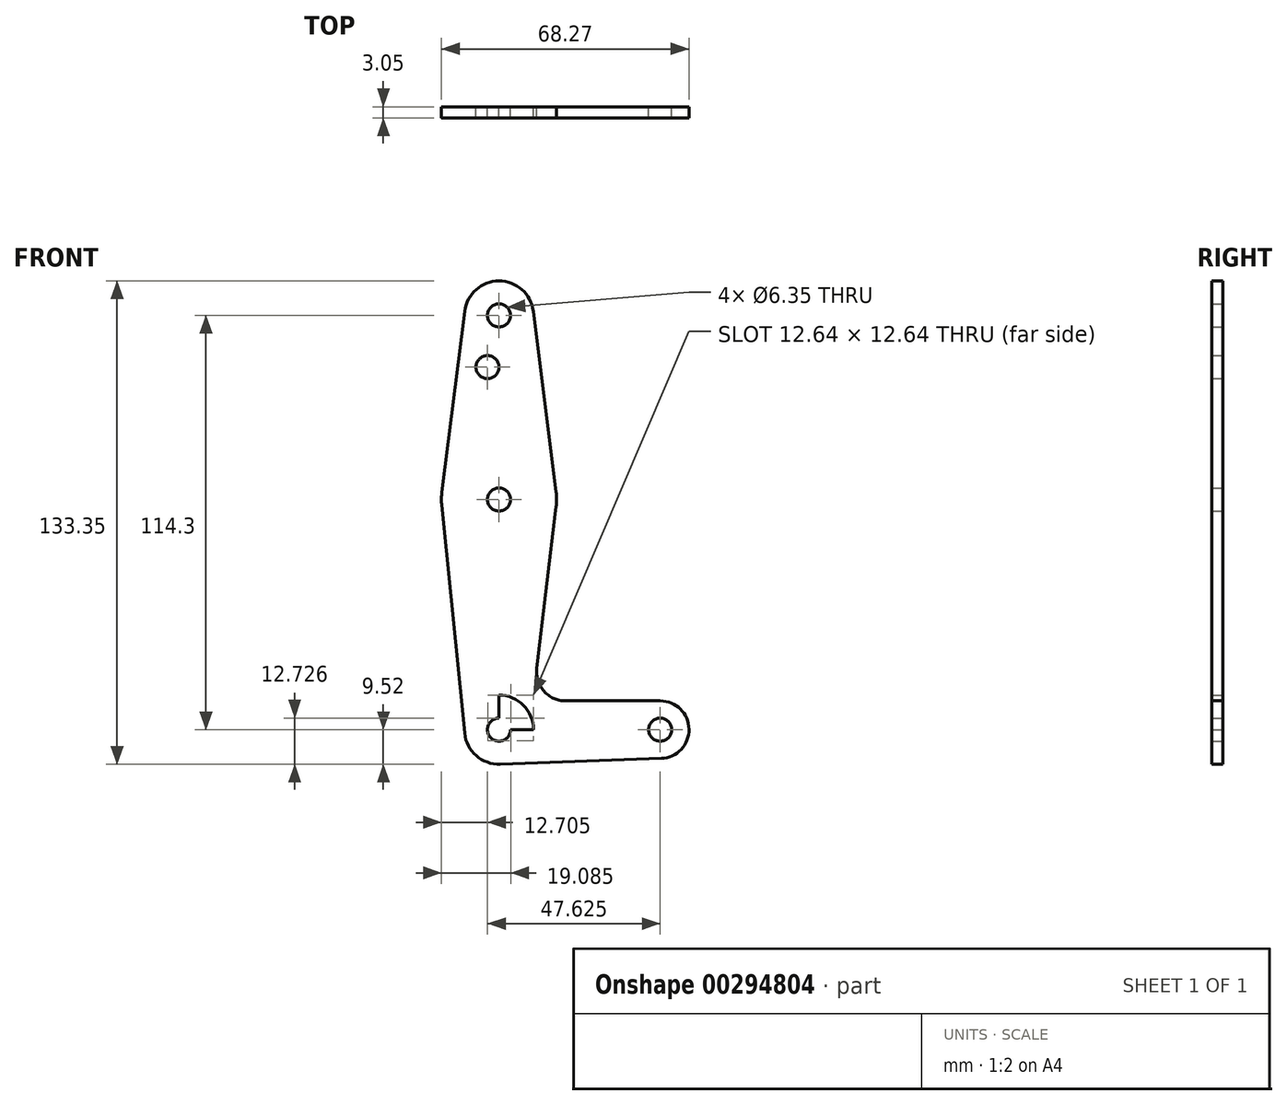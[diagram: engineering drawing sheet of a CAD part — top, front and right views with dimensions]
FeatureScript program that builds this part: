
annotation { "Feature Type Name" : "Feature", "Feature Type Description" : "" }
export const myFeature = defineFeature(function(context is Context, id is Id, definition is map)
    precondition{}
    {
        {
            var Q0;
            Q0=qCreatedBy(makeId("Front.planeOp"),FACE);
            var sketch = newSketch(context, id + "F0", { "sketchPlane" : qUnion([Q0])});
            skCircle(sketch, "E0", {"center": v(0, 114.3) * mm, "radius": 9.53 * mm});
            skCircle(sketch, "E1", {"center": v(0, 63.5) * mm, "radius": 15.88 * mm});
            skCircle(sketch, "E2", {"center": v(44.45, 0) * mm, "radius": 7.94 * mm});
            skLineSegment(sketch, "E3", {"start": v(44.45, 0) * mm, "end": v(0, 0) * mm});
            skLineSegment(sketch, "E4", {"start": v(0, 0) * mm, "end": v(0, 63.5) * mm});
            skLineSegment(sketch, "E5", {"start": v(0, 63.5) * mm, "end": v(0, 114.3) * mm});
            skLineSegment(sketch, "E6", {"start": v(15.76, 61.62) * mm, "end": v(10.43, 16.83) * mm});
            skLineSegment(sketch, "E7", {"start": v(18.32, 7.94) * mm, "end": v(44.45, 7.94) * mm});
            skArc(sketch, "E8.filletArc", {"start": v(10.43, 16.83) * mm, "mid": v(12.38, 10.6) * mm, "end": v(18.32, 7.94) * mm});
            skCircle(sketch, "E9", {"center": v(0, 114.3) * mm, "radius": 3.18 * mm});
            skCircle(sketch, "E10", {"center": v(0, 0) * mm, "radius": 9.53 * mm});
            skCircle(sketch, "E11", {"center": v(44.45, 0) * mm, "radius": 3.18 * mm});
            skLineSegment(sketch, "E12", {"start": v(44.73, -7.93) * mm, "end": v(0.34, -9.52) * mm});
            skLineSegment(sketch, "E13", {"start": v(9.45, 115.5) * mm, "end": v(15.75, 65.48) * mm});
            skLineSegment(sketch, "E14", {"start": v(-9.45, 115.5) * mm, "end": v(-15.75, 65.48) * mm});
            skLineSegment(sketch, "E15", {"start": v(-15.8, 61.91) * mm, "end": v(-9.48, -0.95) * mm});
            skCircle(sketch, "E16", {"center": v(0, 0) * mm, "radius": 3.18 * mm});
            skCircle(sketch, "E17", {"center": v(0, 63.5) * mm, "radius": 3.18 * mm});
            skCircle(sketch, "E18", {"center": v(-3.17, 100.03) * mm, "radius": 3.17 * mm});
            skSolve(sketch);
        }
        {
            var Q0;
            Q0 = qSketchRegion(id + "F0", true);
            extrude(context, id + "F1", {"entities" : qUnion([Q0]), "depth" : 3.05 * mm});
        }
    });
